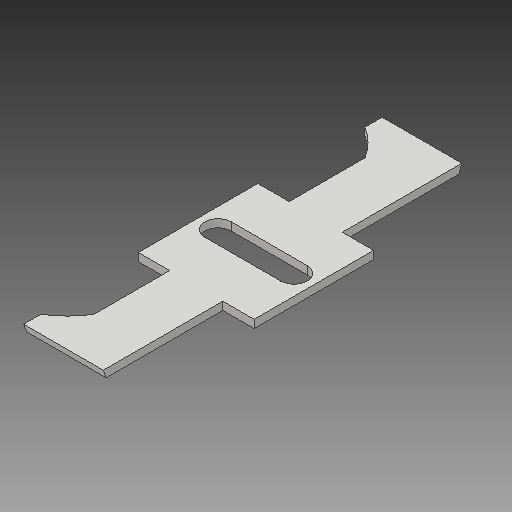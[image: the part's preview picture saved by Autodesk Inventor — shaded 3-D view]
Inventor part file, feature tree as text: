
AUTODESK INVENTOR PART (.ipt)
format: ipt  version: 2017 (Build 210142000, 142)  size: 145,920 bytes
history: native  units: mm
features: draft x2, sketch x2, extrude x1
ambient origin geometry x8: Origin, YZ Plane, XZ Plane, XY Plane, X Axis, Y Axis, Z Axis, Center Point
bodies: Solid1 (feature_tree), Body (feature_tree)
feature tree (5):
  extrude  "Extrusion2"  Depth=30.0mm
  draft  "FaceDraft1"
  draft  "FaceDraft2"
  sketch  "Sketch1"  dims[d16=10.0mm d17=30.0mm]
  sketch  "Sketch2"  dims[d18=6.5mm d19=10.0mm d20=20.0mm d23=45.0mm d24=135.0mm d25=43.6mm d26=3.0mm d27=0.0mm d28=28.6mm d30=62.5mm d31=10.0mm d32=3.0mm d33=0.0mm d34=-3.490659mm d35=-3.490659mm]
